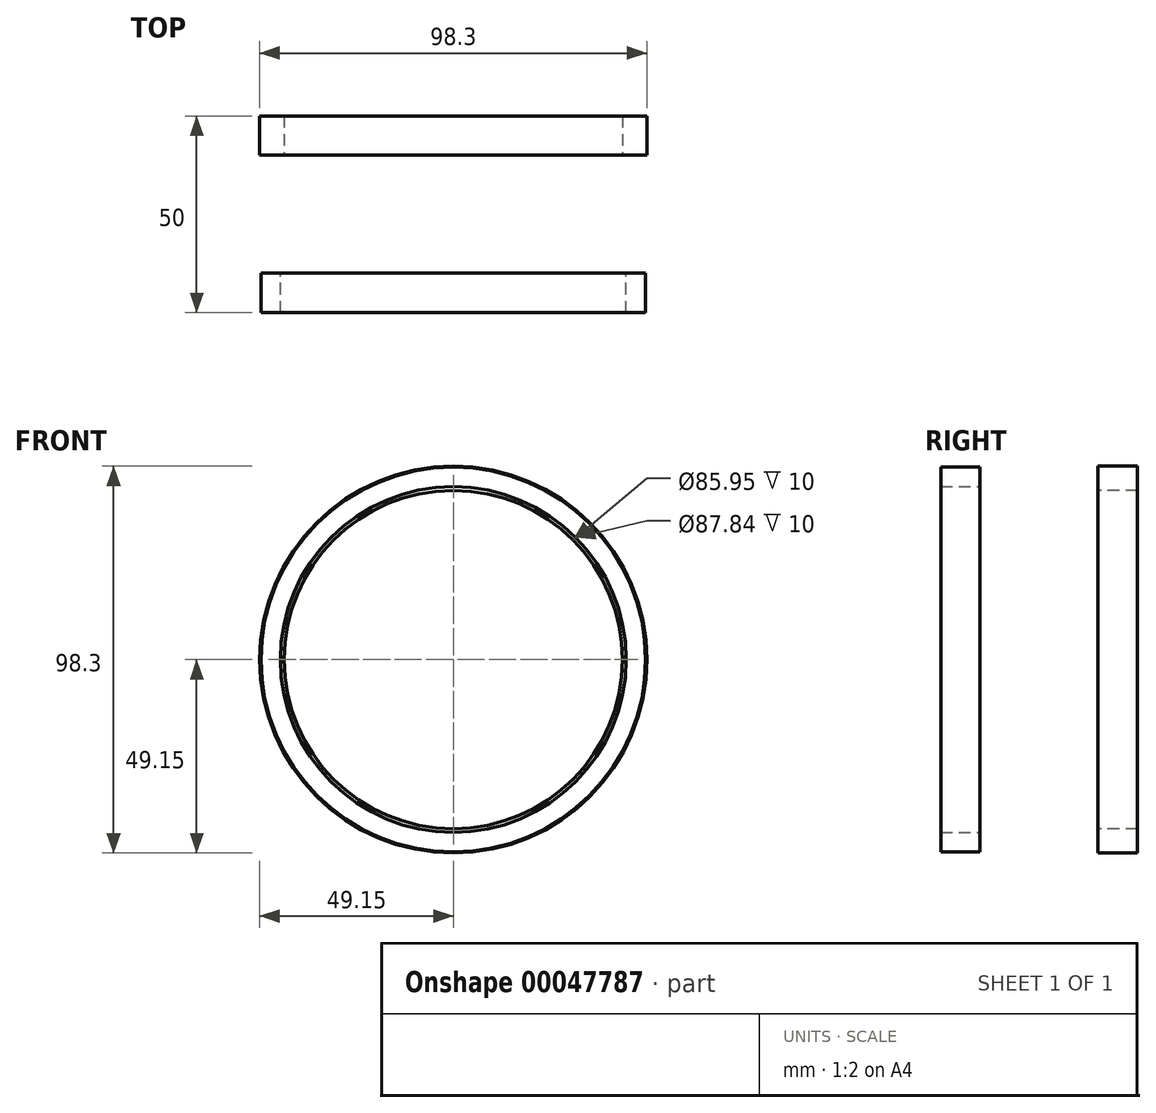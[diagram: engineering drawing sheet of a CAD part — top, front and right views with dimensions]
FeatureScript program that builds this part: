
annotation { "Feature Type Name" : "Feature", "Feature Type Description" : "" }
export const myFeature = defineFeature(function(context is Context, id is Id, definition is map)
    precondition{}
    {
        {
            var Q0;
            Q0=qCreatedBy(makeId("Front.planeOp"),FACE);
            var sketch = newSketch(context, id + "F3", { "sketchPlane" : qUnion([Q0])});
            skCircle(sketch, "E0", {"center": v(0, 0) * mm, "radius": 49.15 * mm});
            skCircle(sketch, "E1", {"center": v(0, 0) * mm, "radius": 42.98 * mm});
            skSolve(sketch);
        }
        {
            var Q0;
            Q0=makeQuery(id+"F3.imprint","IMPRINT",FACE,{"disambiguationData":[TD([[makeQuery(id+"F3.imprint","IMPRINT",EDGE,{"derivedFrom":sQuery(id+"F3.wireOp",EDGE,"E0")}),1.0]])]});
            var sketch = newSketch(context, id + "F4", { "sketchPlane" : qUnion([Q0])});
            skLineSegment(sketch, "E2", {"start": v(9.76, -41.24) * mm, "end": v(9.76, -47.96) * mm});
            skSolve(sketch);
        }
        {
            var Q0;
            Q0=qCreatedBy(makeId("Front.planeOp"),FACE);
            cPlane(context, id + "F0", {"entities" : qUnion([Q0]), "cplaneType" : CPlaneType.OFFSET, "offset" : 30 * mm, "width" : 152.4 * mm, "height" : 152.4 * mm});
        }
        {
            var Q0;
            Q0=qCreatedBy(id+"F0.planeOp",FACE);
            var sketch = newSketch(context, id + "F1", { "sketchPlane" : qUnion([Q0])});
            skCircle(sketch, "E3", {"center": v(0, 0) * mm, "radius": 48.88 * mm});
            skCircle(sketch, "E4", {"center": v(0, 0) * mm, "radius": 43.92 * mm});
            skLineSegment(sketch, "E5", {"start": v(-11.06, -42.5) * mm, "end": v(-11.06, -47.61) * mm});
            skLineSegment(sketch, "E6", {"start": v(-11.06, -47.61) * mm, "end": v(-16.73, -64.09) * mm});
            skSolve(sketch);
        }
        {
            var Q0;
            Q0=makeQuery(id+"F4.imprint","IMPRINT",FACE,{"disambiguationData":[TD([[makeQuery(id+"F4.imprint","IMPRINT",EDGE,{"derivedFrom":makeQuery(id+"F3.imprint","IMPRINT",EDGE,{"derivedFrom":sQuery(id+"F3.wireOp",EDGE,"E0")})}),1.0]])]});
            extrude(context, id + "F2", {"entities" : qUnion([Q0]), "oppositeDirection" : true, "depth" : 10 * mm});
        }
        {
            var Q0;
            Q0=makeQuery(id+"F1.imprint","IMPRINT",FACE,{"disambiguationData":[TD([[makeQuery(id+"F1.imprint","IMPRINT",EDGE,{"derivedFrom":sQuery(id+"F1.wireOp",EDGE,"E3")}),1.0]])]});
            extrude(context, id + "F5", {"entities" : qUnion([Q0]), "depth" : 10 * mm});
        }
    });
